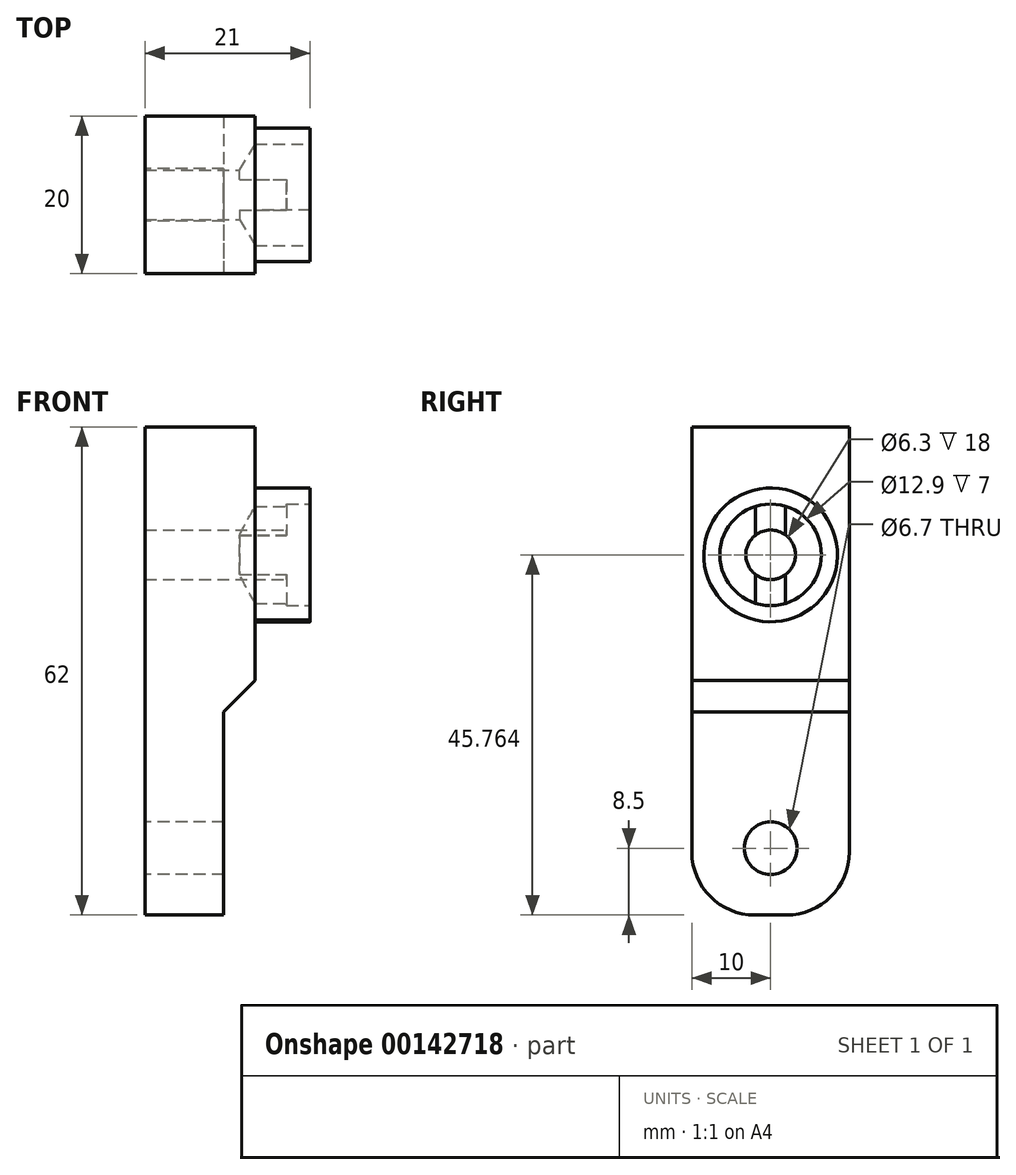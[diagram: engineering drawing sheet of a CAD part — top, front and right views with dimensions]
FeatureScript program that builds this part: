
annotation { "Feature Type Name" : "Feature", "Feature Type Description" : "" }
export const myFeature = defineFeature(function(context is Context, id is Id, definition is map)
    precondition{}
    {
        {
            var Q0;
            Q0=qCreatedBy(makeId("Right.planeOp"),FACE);
            var sketch = newSketch(context, id + "F0", { "sketchPlane" : qUnion([Q0])});
            skLineSegment(sketch, "E0.bottom", {"start": v(-20, 0) * mm, "end": v(0, 0) * mm});
            skLineSegment(sketch, "E0.top", {"start": v(-20, -62) * mm, "end": v(0, -62) * mm});
            skLineSegment(sketch, "E0.left", {"start": v(-20, 0) * mm, "end": v(-20, -62) * mm});
            skLineSegment(sketch, "E0.right", {"start": v(0, 0) * mm, "end": v(0, -62) * mm});
            skPoint(sketch, "E1", {"position": v(-10, -53) * mm});
            skSolve(sketch);
        }
        {
            var Q0;
            Q0 = qSketchRegion(id + "F0", true);
            extrude(context, id + "F1", {"entities" : qUnion([Q0]), "depth" : 14 * mm});
        }
        {
            var Q0;
            Q0=makeQuery(id+"F1.opExtrude","CAP_FACE",FACE,{"disambiguationData":[OSD([sQuery(id+"F0.wireOp",EDGE,"E0.bottom"),sQuery(id+"F0.wireOp",EDGE,"E0.top"),sQuery(id+"F0.wireOp",EDGE,"E0.left"),sQuery(id+"F0.wireOp",EDGE,"E0.right")])],"isStart":false});
            var sketch = newSketch(context, id + "F2", { "sketchPlane" : qUnion([Q0])});
            skCircle(sketch, "E2", {"center": v(-10, -16.24) * mm, "radius": 8.5 * mm});
            skSolve(sketch);
        }
        {
            var Q0;
            Q0 = qSketchRegion(id + "F2", true);
            extrude(context, id + "F3", {"entities" : qUnion([Q0]), "operationType" : NewBodyOperationType.ADD, "depth" : 7 * mm});
        }
        {
            var Q0;
            Q0=makeQuery(id+"F3.opExtrude","CAP_FACE",FACE,{"disambiguationData":[OSD([sQuery(id+"F2.wireOp",EDGE,"E2")])],"isStart":false});
            var sketch = newSketch(context, id + "F4", { "sketchPlane" : qUnion([Q0])});
            skPoint(sketch, "E3", {"position": v(-10, -16.24) * mm});
            skSolve(sketch);
        }
        {
            var Q0;
            Q0=sQuery(id+"F4.wireOp",VERTEX,"E3");
            var Q1;
            Q1=makeQuery(id+"F1.opExtrude","SWEPT_BODY",BODY,{"disambiguationData":[OSD([sQuery(id+"F0.wireOp",EDGE,"E0.bottom"),sQuery(id+"F0.wireOp",EDGE,"E0.top"),sQuery(id+"F0.wireOp",EDGE,"E0.left"),sQuery(id+"F0.wireOp",EDGE,"E0.right")])]});
            hole(context, id + "F5", {"style" : HoleStyle.SIMPLE, "endStyle" : HoleEndStyle.BLIND, "holeDiameter" : 12.9 * mm, "holeDepth" : 7 * mm, "locations" : qUnion([Q0]), "scope" : qUnion([Q1])});
        }
        {
            var Q0;
            Q0=makeQuery(id+"F3.opExtrude","CAP_FACE",FACE,{"disambiguationData":[OSD([sQuery(id+"F2.wireOp",EDGE,"E2")])],"isStart":false});
            var sketch = newSketch(context, id + "F6", { "sketchPlane" : qUnion([Q0])});
            skLineSegment(sketch, "E4.bottom", {"start": v(-8.09, -24.52) * mm, "end": v(-11.94, -24.52) * mm});
            skLineSegment(sketch, "E4.top", {"start": v(-8.09, -7.96) * mm, "end": v(-11.94, -7.96) * mm});
            skLineSegment(sketch, "E4.left", {"start": v(-8.09, -24.52) * mm, "end": v(-8.09, -7.96) * mm});
            skLineSegment(sketch, "E4.right", {"start": v(-11.94, -24.52) * mm, "end": v(-11.94, -7.96) * mm});
            skSolve(sketch);
        }
        {
            var Q0;
            Q0 = qSketchRegion(id + "F6", true);
            extrude(context, id + "F7", {"entities" : qUnion([Q0]), "operationType" : NewBodyOperationType.ADD, "oppositeDirection" : true, "depth" : 11.6 * mm});
        }
        {
            var Q0;
            Q0=makeQuery(id+"F7.boolean.opBoolean","MERGE",FACE,{"derivedFrom":[makeQuery(id+"F3.opExtrude","CAP_FACE",FACE,{"disambiguationData":[OSD([sQuery(id+"F2.wireOp",EDGE,"E2")])],"isStart":false}),makeQuery(id+"F7.opExtrude","CAP_FACE",FACE,{"disambiguationData":[OSD([sQuery(id+"F6.wireOp",EDGE,"E4.bottom"),sQuery(id+"F6.wireOp",EDGE,"E4.top"),sQuery(id+"F6.wireOp",EDGE,"E4.left"),sQuery(id+"F6.wireOp",EDGE,"E4.right")])],"isStart":true})]});
            var sketch = newSketch(context, id + "F8", { "sketchPlane" : qUnion([Q0])});
            skPoint(sketch, "E5", {"position": v(-10, -16.24) * mm});
            skSolve(sketch);
        }
        {
            var Q0;
            Q0=sQuery(id+"F8.wireOp",VERTEX,"E5");
            var Q1;
            Q1=makeQuery(id+"F1.opExtrude","SWEPT_BODY",BODY,{"disambiguationData":[OSD([sQuery(id+"F0.wireOp",EDGE,"E0.bottom"),sQuery(id+"F0.wireOp",EDGE,"E0.top"),sQuery(id+"F0.wireOp",EDGE,"E0.left"),sQuery(id+"F0.wireOp",EDGE,"E0.right")])]});
            hole(context, id + "F9", {"style" : HoleStyle.SIMPLE, "endStyle" : HoleEndStyle.THROUGH, "holeDiameter" : 6.3 * mm, "locations" : qUnion([Q0]), "scope" : qUnion([Q1]), "isTappedThrough" : true});
        }
        {
            var Q0;
            Q0=makeQuery(id+"F7.boolean.opBoolean","MERGE",FACE,{"derivedFrom":[makeQuery(id+"F3.opExtrude","CAP_FACE",FACE,{"disambiguationData":[OSD([sQuery(id+"F2.wireOp",EDGE,"E2")])],"isStart":false}),makeQuery(id+"F7.opExtrude","CAP_FACE",FACE,{"disambiguationData":[OSD([sQuery(id+"F6.wireOp",EDGE,"E4.bottom"),sQuery(id+"F6.wireOp",EDGE,"E4.top"),sQuery(id+"F6.wireOp",EDGE,"E4.left"),sQuery(id+"F6.wireOp",EDGE,"E4.right")])],"isStart":true})]});
            var sketch = newSketch(context, id + "F10", { "sketchPlane" : qUnion([Q0])});
            skCircle(sketch, "E6", {"center": v(-10, -16.24) * mm, "radius": 6.45 * mm});
            skSolve(sketch);
        }
        {
            var Q0;
            Q0 = qSketchRegion(id + "F10", true);
            extrude(context, id + "F11", {"entities" : qUnion([Q0]), "operationType" : NewBodyOperationType.REMOVE, "oppositeDirection" : true, "depth" : 3 * mm});
        }
        {
            var Q0;
            Q0=makeQuery(id+"F1.opExtrude","SWEPT_EDGE",EDGE,{"disambiguationData":[OSD([sQuery(id+"F0.wireOp",EDGE,"E0.top"),sQuery(id+"F0.wireOp",EDGE,"E0.right")])]});
            fillet(context, id + "F12", {"entities" : qUnion([Q0]), "radius" : 8 * mm, "tangentPropagation" : true, "allowEdgeOverflow" : false});
        }
        {
            var Q0;
            Q0=makeQuery(id+"F1.opExtrude","SWEPT_EDGE",EDGE,{"disambiguationData":[OSD([sQuery(id+"F0.wireOp",EDGE,"E0.top"),sQuery(id+"F0.wireOp",EDGE,"E0.left")])]});
            fillet(context, id + "F13", {"entities" : qUnion([Q0]), "radius" : 8 * mm, "tangentPropagation" : true, "allowEdgeOverflow" : false});
        }
        {
            var Q0;
            Q0=makeQuery(id+"F1.opExtrude","SWEPT_FACE",FACE,{"disambiguationData":[OSD([sQuery(id+"F0.wireOp",EDGE,"E0.left")])]});
            var sketch = newSketch(context, id + "F14", { "sketchPlane" : qUnion([Q0])});
            skLineSegment(sketch, "E7.bottom", {"start": v(14, -32.2) * mm, "end": v(10, -32.2) * mm});
            skLineSegment(sketch, "E7.top", {"start": v(14, -69.3) * mm, "end": v(10, -69.3) * mm});
            skLineSegment(sketch, "E7.left", {"start": v(14, -32.2) * mm, "end": v(14, -69.3) * mm});
            skLineSegment(sketch, "E7.right", {"start": v(10, -32.2) * mm, "end": v(10, -69.3) * mm});
            skSolve(sketch);
        }
        {
            var Q0;
            Q0 = qSketchRegion(id + "F14", true);
            extrude(context, id + "F15", {"entities" : qUnion([Q0]), "operationType" : NewBodyOperationType.REMOVE, "oppositeDirection" : true, "depth" : 25 * mm});
        }
        {
            var Q0;
            Q0=makeQuery(id+"F1.opExtrude","CAP_FACE",FACE,{"disambiguationData":[OSD([sQuery(id+"F0.wireOp",EDGE,"E0.bottom"),sQuery(id+"F0.wireOp",EDGE,"E0.top"),sQuery(id+"F0.wireOp",EDGE,"E0.left"),sQuery(id+"F0.wireOp",EDGE,"E0.right")])],"isStart":true});
            var sketch = newSketch(context, id + "F16", { "sketchPlane" : qUnion([Q0])});
            skPoint(sketch, "E8", {"position": v(10, -53.5) * mm});
            skSolve(sketch);
        }
        {
            var Q0;
            Q0=sQuery(id+"F16.wireOp",VERTEX,"E8");
            var Q1;
            Q1=makeQuery(id+"F1.opExtrude","SWEPT_BODY",BODY,{"disambiguationData":[OSD([sQuery(id+"F0.wireOp",EDGE,"E0.bottom"),sQuery(id+"F0.wireOp",EDGE,"E0.top"),sQuery(id+"F0.wireOp",EDGE,"E0.left"),sQuery(id+"F0.wireOp",EDGE,"E0.right")])]});
            hole(context, id + "F17", {"style" : HoleStyle.SIMPLE, "endStyle" : HoleEndStyle.THROUGH, "holeDiameter" : 6.7 * mm, "locations" : qUnion([Q0]), "scope" : qUnion([Q1]), "isTappedThrough" : true});
        }
        {
            var Q0;
            Q0=makeQuery(id+"F15.boolean.opBoolean","COPY",EDGE,{"derivedFrom":makeQuery(id+"F15.opExtrude","SWEPT_EDGE",EDGE,{"disambiguationData":[OSD([sQuery(id+"F14.wireOp",EDGE,"E7.bottom"),sQuery(id+"F14.wireOp",EDGE,"E7.right")])]})});
            chamfer(context, id + "F18", {"entities" : qUnion([Q0]), "width" : 4 * mm, "tangentPropagation" : true});
        }
    });
